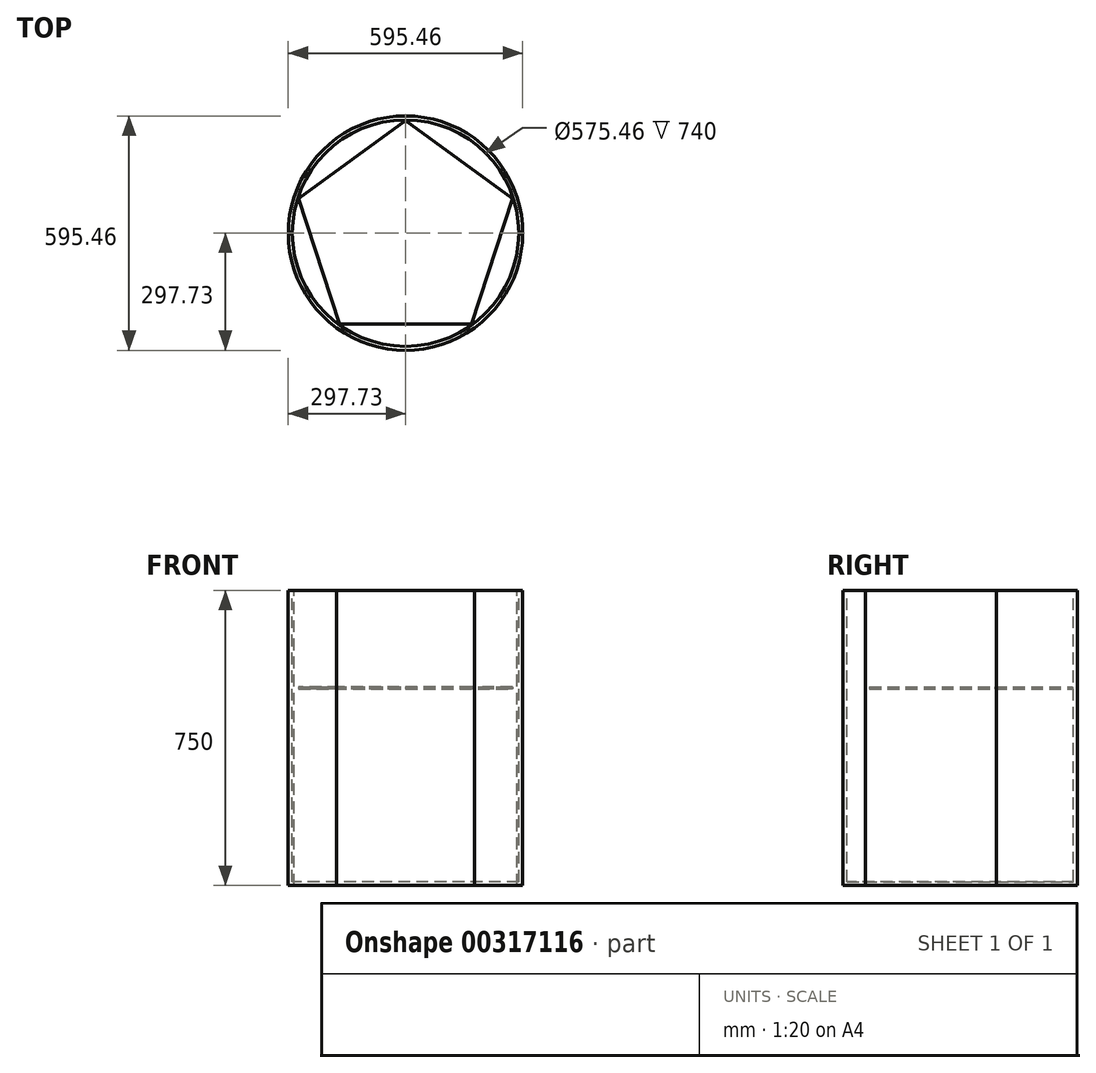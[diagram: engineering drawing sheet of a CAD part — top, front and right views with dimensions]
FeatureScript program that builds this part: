
annotation { "Feature Type Name" : "Feature", "Feature Type Description" : "" }
export const myFeature = defineFeature(function(context is Context, id is Id, definition is map)
    precondition{}
    {
        {
            var Q0;
            Q0=qCreatedBy(makeId("Top.planeOp"),FACE);
            var sketch = newSketch(context, id + "F0", { "sketchPlane" : qUnion([Q0])});
            skCircle(sketch, "E0.cCircle", {"center": v(0, 0) * mm, "radius": 240.87 * mm, "construction": true});
            skLineSegment(sketch, "E0.0", {"start": v(0, 297.73) * mm, "end": v(283.16, 92) * mm});
            skLineSegment(sketch, "E0.1", {"start": v(283.16, 92) * mm, "end": v(175, -240.87) * mm});
            skLineSegment(sketch, "E0.2", {"start": v(175, -240.87) * mm, "end": v(-175, -240.87) * mm});
            skLineSegment(sketch, "E0.3", {"start": v(-175, -240.87) * mm, "end": v(-283.16, 92) * mm});
            skLineSegment(sketch, "E0.4", {"start": v(-283.16, 92) * mm, "end": v(0, 297.73) * mm});
            skPoint(sketch, "E0.0.midPoint", {"position": v(141.58, 194.87) * mm});
            skLineSegment(sketch, "E1", {"start": v(0, 0) * mm, "end": v(0, 297.73) * mm, "construction": true});
            skLineSegment(sketch, "E2", {"start": v(0, 0) * mm, "end": v(283.16, 92) * mm, "construction": true});
            skLineSegment(sketch, "E3", {"start": v(0, 0) * mm, "end": v(175, -240.87) * mm, "construction": true});
            skLineSegment(sketch, "E4", {"start": v(0, 0) * mm, "end": v(-175, -240.87) * mm, "construction": true});
            skLineSegment(sketch, "E5", {"start": v(0, 0) * mm, "end": v(-283.16, 92) * mm, "construction": true});
            skLineSegment(sketch, "E6", {"start": v(-283.16, 92) * mm, "end": v(229.08, -74.43) * mm, "construction": true});
            skLineSegment(sketch, "E7.bottom", {"start": v(283.16, 302.3) * mm, "end": v(-283.16, 302.3) * mm, "construction": true});
            skLineSegment(sketch, "E7.top", {"start": v(283.16, -243.17) * mm, "end": v(-283.16, -243.17) * mm, "construction": true});
            skLineSegment(sketch, "E7.left", {"start": v(283.16, 302.3) * mm, "end": v(283.16, -243.17) * mm, "construction": true});
            skLineSegment(sketch, "E7.right", {"start": v(-283.16, 302.3) * mm, "end": v(-283.16, -243.17) * mm, "construction": true});
            skPoint(sketch, "E7.middle", {"position": v(0, 29.57) * mm});
            skCircle(sketch, "E8", {"center": v(0, 0) * mm, "radius": 297.73 * mm});
            skSolve(sketch);
        }
        {
            var Q0;
            Q0 = qSketchRegion(id + "F0", true);
            extrude(context, id + "F1", {"entities" : qUnion([Q0]), "oppositeDirection" : true, "depth" : 750 * mm});
        }
        {
            var Q0;
            Q0=makeQuery(id+"F1.opExtrude","CAP_FACE",FACE,{"disambiguationData":[OSD([sQuery(id+"F0.wireOp",EDGE,"E0.0"),sQuery(id+"F0.wireOp",EDGE,"E0.1"),sQuery(id+"F0.wireOp",EDGE,"E0.2"),sQuery(id+"F0.wireOp",EDGE,"E0.3"),sQuery(id+"F0.wireOp",EDGE,"E0.4")])],"isStart":true});
            shell(context, id + "F2", {"entities" : qUnion([Q0]), "thickness" : 10 * mm});
        }
        {
            var Q0;
            Q0=qCreatedBy(makeId("Top.planeOp"),FACE);
            cPlane(context, id + "F3", {"entities" : qUnion([Q0]), "cplaneType" : CPlaneType.OFFSET, "offset" : 250 * mm, "oppositeDirection" : true, "width" : 150 * mm, "height" : 150 * mm});
        }
        {
            var Q0;
            Q0=qCreatedBy(id+"F3.planeOp",FACE);
            var sketch = newSketch(context, id + "F4", { "sketchPlane" : qUnion([Q0])});
            skLineSegment(sketch, "E9.0", {"start": v(-271.4, 88.18) * mm, "end": v(0, 285.37) * mm});
            skLineSegment(sketch, "E9.1", {"start": v(-167.73, -230.87) * mm, "end": v(-271.4, 88.18) * mm});
            skLineSegment(sketch, "E9.2", {"start": v(167.73, -230.87) * mm, "end": v(-167.73, -230.87) * mm});
            skLineSegment(sketch, "E9.3", {"start": v(0, 285.37) * mm, "end": v(271.4, 88.18) * mm});
            skLineSegment(sketch, "E9.4", {"start": v(271.4, 88.18) * mm, "end": v(167.73, -230.87) * mm});
            skSolve(sketch);
        }
        {
            var Q0;
            Q0 = qSketchRegion(id + "F4", true);
            extrude(context, id + "F5", {"entities" : qUnion([Q0]), "operationType" : NewBodyOperationType.ADD, "depth" : 5 * mm});
        }
    });
